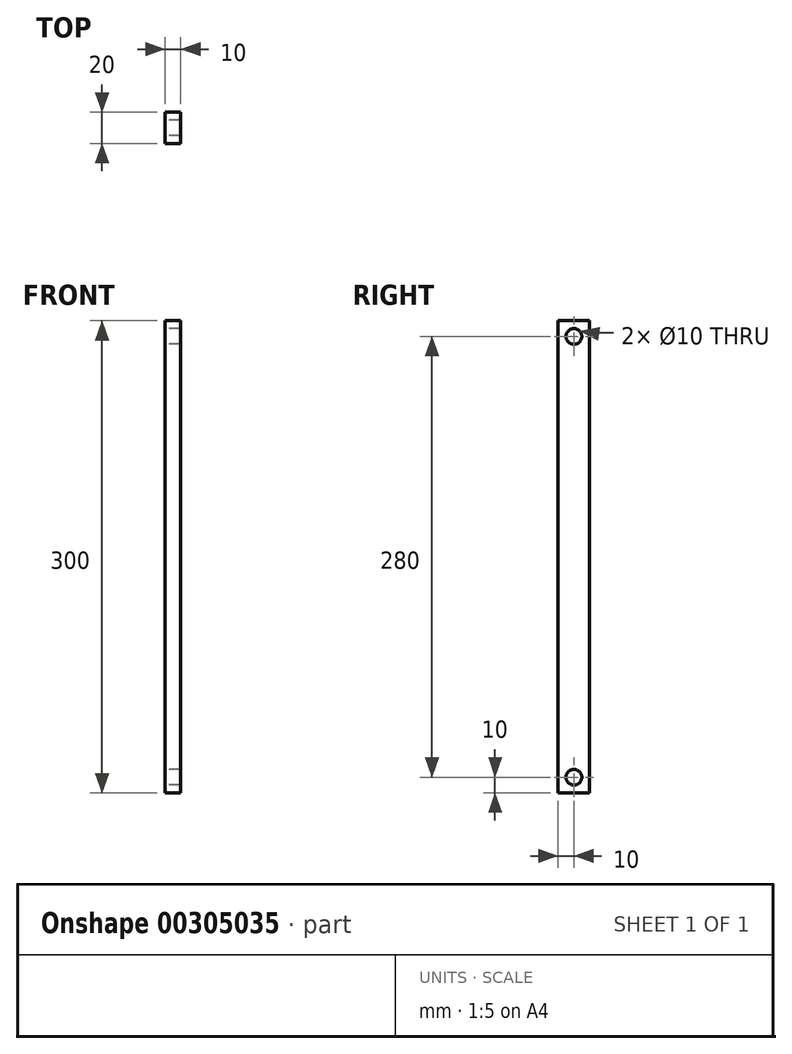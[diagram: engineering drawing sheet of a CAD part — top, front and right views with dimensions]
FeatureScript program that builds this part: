
annotation { "Feature Type Name" : "Feature", "Feature Type Description" : "" }
export const myFeature = defineFeature(function(context is Context, id is Id, definition is map)
    precondition{}
    {
        {
            var Q0;
            Q0=qCreatedBy(makeId("Right.planeOp"),FACE);
            var sketch = newSketch(context, id + "F0", { "sketchPlane" : qUnion([Q0])});
            skLineSegment(sketch, "E0.bottom", {"start": v(0, 0) * mm, "end": v(20, 0) * mm});
            skLineSegment(sketch, "E0.top", {"start": v(0, 300) * mm, "end": v(20, 300) * mm});
            skLineSegment(sketch, "E0.left", {"start": v(0, 0) * mm, "end": v(0, 300) * mm});
            skLineSegment(sketch, "E0.right", {"start": v(20, 0) * mm, "end": v(20, 300) * mm});
            skCircle(sketch, "E1", {"center": v(10, 290) * mm, "radius": 5 * mm});
            skCircle(sketch, "E2", {"center": v(10, 10) * mm, "radius": 5 * mm});
            skSolve(sketch);
        }
        {
            var Q0;
            Q0 = qSketchRegion(id + "F0", true);
            extrude(context, id + "F1", {"entities" : qUnion([Q0]), "depth" : 10 * mm});
        }
    });
